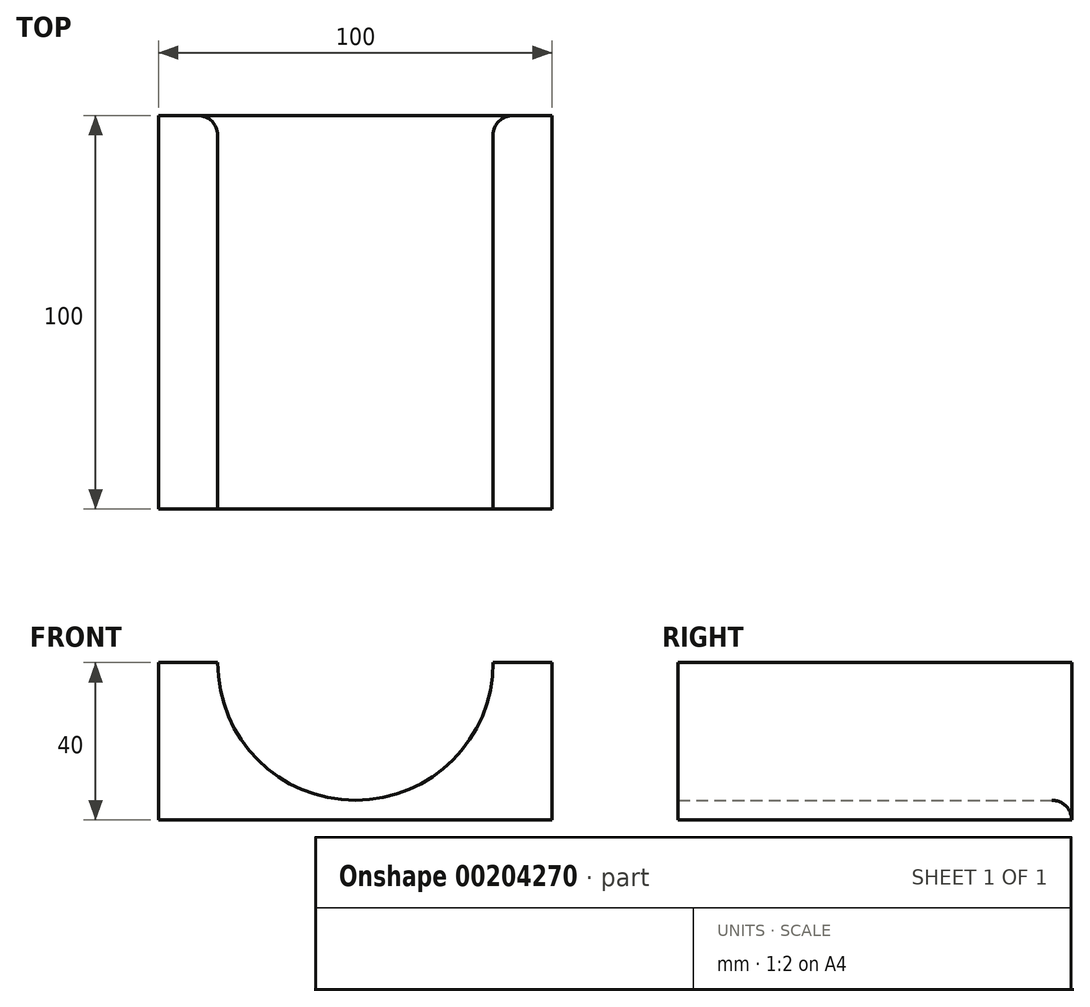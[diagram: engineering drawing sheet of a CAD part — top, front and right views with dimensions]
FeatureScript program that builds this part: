
annotation { "Feature Type Name" : "Feature", "Feature Type Description" : "" }
export const myFeature = defineFeature(function(context is Context, id is Id, definition is map)
    precondition{}
    {
        {
            var Q0;
            Q0=qCreatedBy(makeId("Front.planeOp"),FACE);
            var sketch = newSketch(context, id + "F0", { "sketchPlane" : qUnion([Q0])});
            skLineSegment(sketch, "E0.bottom", {"start": v(-50, 0) * mm, "end": v(0, 0) * mm});
            skLineSegment(sketch, "E0.top", {"start": v(-50, 40) * mm, "end": v(0, 40) * mm});
            skLineSegment(sketch, "E0.left", {"start": v(-50, 0) * mm, "end": v(-50, 40) * mm});
            skLineSegment(sketch, "E1.MirrorCS", {"start": v(50, 0) * mm, "end": v(0, 0) * mm});
            skLineSegment(sketch, "E2.MirrorCS", {"start": v(50, 0) * mm, "end": v(50, 40) * mm});
            skLineSegment(sketch, "E3.MirrorCS", {"start": v(50, 40) * mm, "end": v(0, 40) * mm});
            skArc(sketch, "E4", {"start": v(-35, 40) * mm, "mid": v(0, 5) * mm, "end": v(35, 40) * mm});
            skSolve(sketch);
        }
        {
            var Q0;
            Q0=makeQuery(id+"F0.imprint","IMPRINT",FACE,{"disambiguationData":[TD([[makeQuery(id+"F0.imprint","IMPRINT",EDGE,{"derivedFrom":sQuery(id+"F0.wireOp",EDGE,"E0.bottom")}),1.0]])]});
            extrude(context, id + "F1", {"entities" : qUnion([Q0]), "endBound" : BoundingType.SYMMETRIC, "depth" : 100 * mm});
        }
        {
            var Q0;
            Q0=makeQuery(id+"F1.opExtrude","CAP_EDGE",EDGE,{"disambiguationData":[OSD([sQuery(id+"F0.wireOp",EDGE,"E4")])],"isStart":true});
            fillet(context, id + "F2", {"entities" : qUnion([Q0]), "radius" : 5 * mm, "tangentPropagation" : true, "allowEdgeOverflow" : false});
        }
    });
